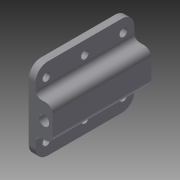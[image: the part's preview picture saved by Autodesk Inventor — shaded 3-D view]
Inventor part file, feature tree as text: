
AUTODESK INVENTOR PART (.ipt)
format: ipt  version: 2015 (Build 190159000, 159)  size: 151,552 bytes
history: native  units: in
note: dims shown in document units (in); Inventor stores cm internally (conversion verified against a paired STEP export)
features: extrude x4, sketch x4, fillet x3, projected_geometry x2
ambient origin geometry x8: Origin, YZ Plane, XZ Plane, XY Plane, X Axis, Y Axis, Z Axis, Center Point
bodies: Solid1 (feature_tree)
feature tree (13):
  extrude  "Extrusion1"  Depth=1.815in
  extrude  "Extrusion2"  Depth=0.125in TaperAngle=0.0deg
  extrude  "Extrusion3"  Depth=0.3125in
  extrude  "Extrusion4"  Depth=0.125in
  fillet  "Fillet1"  Radius=0.1in
  fillet  "Fillet2"  Radius=0.225in
  fillet  "Fillet4"  Radius=0.1406in
  sketch  "Sketch1"  dims[d0=1.5in d1=1.815in]
  sketch  "Sketch2"  dims[d2=0.125in d3=0.0in d5=0.125in d6=0.0in]
  projected_geometry  "Projected Loop1"
  sketch  "Sketch3"  dims[d7=0.3125in d8=0.0in d9=0.188in]
  sketch  "Sketch4"  dims[d10=2.0in d11=0.0in d12=0.125in d13=0.1in d15=0.225in d16=0.1406in]
  projected_geometry  "Projected Loop2"
